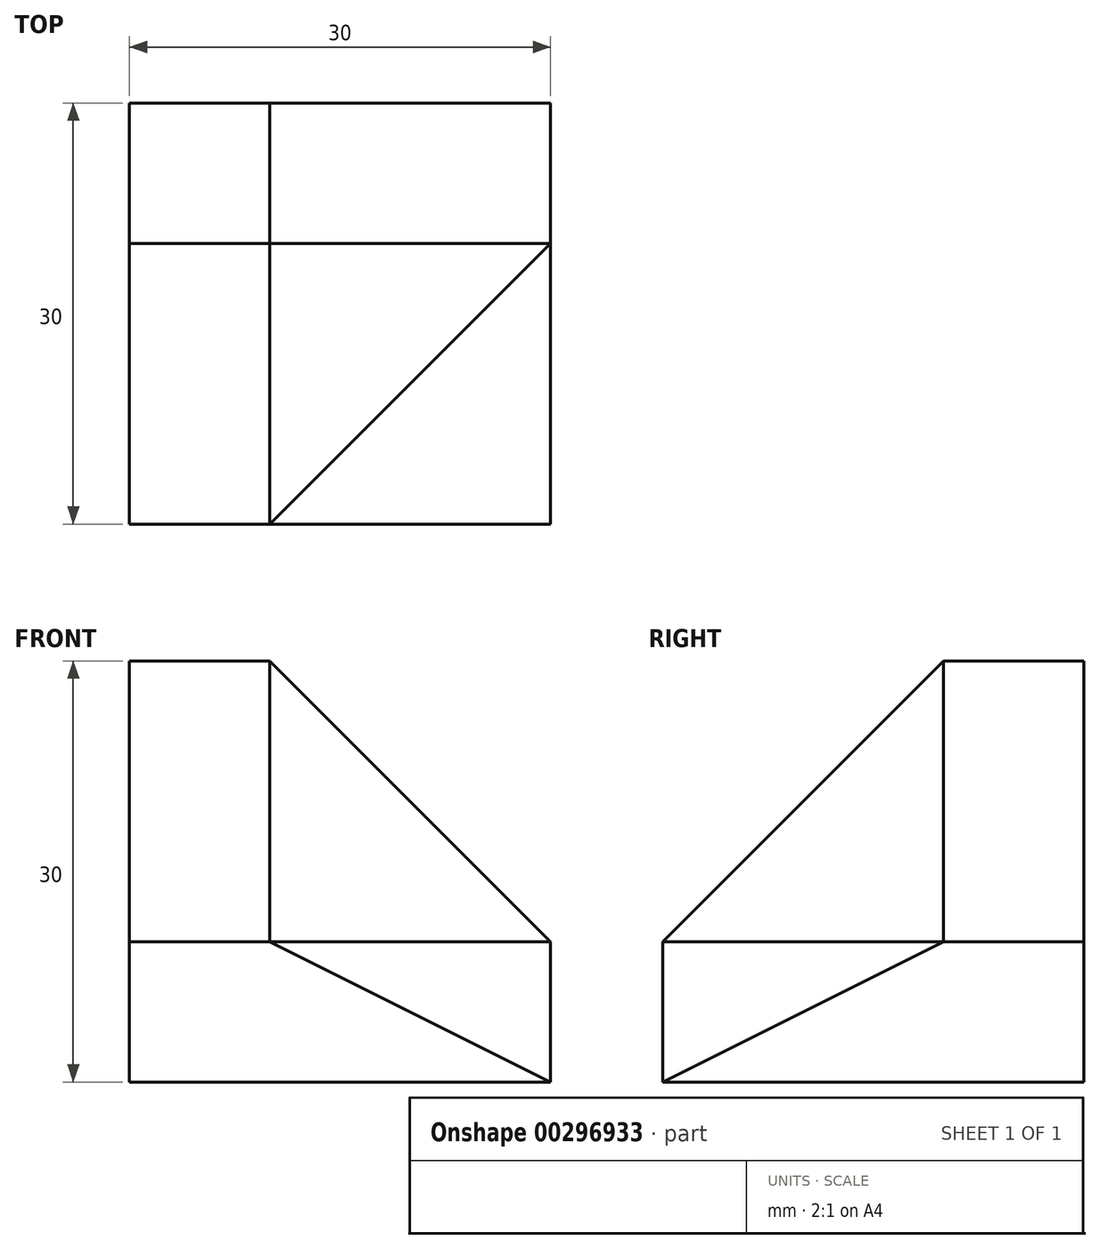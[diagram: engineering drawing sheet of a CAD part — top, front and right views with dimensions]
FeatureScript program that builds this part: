
annotation { "Feature Type Name" : "Feature", "Feature Type Description" : "" }
export const myFeature = defineFeature(function(context is Context, id is Id, definition is map)
    precondition{}
    {
        {
            var Q0;
            Q0=qCreatedBy(makeId("Front.planeOp"),FACE);
            var sketch = newSketch(context, id + "F0", { "sketchPlane" : qUnion([Q0])});
            skLineSegment(sketch, "E0.bottom", {"start": v(0, 0) * mm, "end": v(30, 0) * mm});
            skLineSegment(sketch, "E0.top", {"start": v(0, 30) * mm, "end": v(30, 30) * mm});
            skLineSegment(sketch, "E0.left", {"start": v(0, 0) * mm, "end": v(0, 30) * mm});
            skLineSegment(sketch, "E0.right", {"start": v(30, 0) * mm, "end": v(30, 30) * mm});
            skLineSegment(sketch, "E1", {"start": v(10, 30) * mm, "end": v(30, 10) * mm});
            skLineSegment(sketch, "E2.bottom", {"start": v(30, 30) * mm, "end": v(10, 30) * mm});
            skLineSegment(sketch, "E2.top", {"start": v(30, 10) * mm, "end": v(10, 10) * mm});
            skLineSegment(sketch, "E2.left", {"start": v(30, 30) * mm, "end": v(30, 10) * mm});
            skLineSegment(sketch, "E2.right", {"start": v(10, 30) * mm, "end": v(10, 10) * mm});
            skSolve(sketch);
        }
        {
            var Q0;
            {var subQ1=sQuery(id+"F0.wireOp",EDGE,"E0.bottom");Q0=makeQuery(id+"F0.imprint","IMPRINT",FACE,{"disambiguationData":[TD([[makeQuery(id+"F0.imprint","IMPRINT",EDGE,{"derivedFrom":subQ1}),1.0]])]});}
            var Q1;
            Q1=makeQuery(id+"F0.imprint","IMPRINT",FACE,{"disambiguationData":[TD([[makeQuery(id+"F0.imprint","IMPRINT",EDGE,{"derivedFrom":sQuery(id+"F0.wireOp",EDGE,"E1")}),-1.0]])]});
            extrude(context, id + "F1", {"entities" : qUnion([Q0, Q1]), "oppositeDirection" : true, "depth" : 30 * mm});
        }
        {
            var Q0;
            Q0=makeQuery(id+"F0.imprint","IMPRINT",FACE,{"disambiguationData":[TD([[makeQuery(id+"F0.imprint","IMPRINT",EDGE,{"derivedFrom":sQuery(id+"F0.wireOp",EDGE,"E1")}),-1.0]])]});
            extrude(context, id + "F2", {"entities" : qUnion([Q0]), "operationType" : NewBodyOperationType.REMOVE, "oppositeDirection" : true, "depth" : 20 * mm});
        }
        {
            var Q0;
            Q0=makeQuery(id+"F2.boolean.opBoolean","COPY",FACE,{"derivedFrom":makeQuery(id+"F2.opExtrude","SWEPT_FACE",FACE,{"disambiguationData":[OSD([sQuery(id+"F0.wireOp",EDGE,"E2.right")])]})});
            var sketch = newSketch(context, id + "F3", { "sketchPlane" : qUnion([Q0])});
            skLineSegment(sketch, "E3", {"start": v(20, 30) * mm, "end": v(0, 10) * mm});
            skSolve(sketch);
        }
        {
            var Q0;
            Q0 = qSketchRegion(id + "F3", true);
            var Q1;
            Q1=makeQuery(id+"F3.imprint","IMPRINT",FACE,{"disambiguationData":[TD([[makeQuery(id+"F3.imprint","IMPRINT",EDGE,{"derivedFrom":sQuery(id+"F3.wireOp",EDGE,"E3")}),-1.0]])]});
            extrude(context, id + "F4", {"entities" : qUnion([Q0, Q1]), "operationType" : NewBodyOperationType.REMOVE, "endBound" : BoundingType.THROUGH_ALL, "oppositeDirection" : true, "depth" : 25 * mm});
        }
        {
            var Q0;
            Q0=makeQuery(id+"F2.boolean.opBoolean","COPY",VERTEX,{"derivedFrom":makeQuery(id+"F2.opExtrude","CAP_VERTEX",VERTEX,{"disambiguationData":[OSD([sQuery(id+"F0.wireOp",EDGE,"E0.right"),sQuery(id+"F0.wireOp",EDGE,"E1"),sQuery(id+"F0.wireOp",EDGE,"E2.top"),sQuery(id+"F0.wireOp",EDGE,"E2.left")])],"isStart":false})});
            var Q1;
            {var subQ0=sQuery(id+"F0.wireOp",EDGE,"E2.right");var subQ1=sQuery(id+"F0.wireOp",EDGE,"E2.top");Q1=makeQuery(id+"F4.boolean.opBoolean","MERGE",VERTEX,{"derivedFrom":[makeQuery(id+"F2.boolean.opBoolean","COPY",VERTEX,{"derivedFrom":makeQuery(id+"F2.opExtrude","CAP_VERTEX",VERTEX,{"disambiguationData":[OSD([subQ1,subQ0])],"isStart":true})}),makeQuery(id+"F4.opExtrude","CAP_VERTEX",VERTEX,{"disambiguationData":[OSD([subQ1,subQ0,sQuery(id+"F3.wireOp",EDGE,"E3")])],"isStart":true})]});}
            var Q2;
            Q2=makeQuery(id+"F1.opExtrude","CAP_VERTEX",VERTEX,{"disambiguationData":[OSD([sQuery(id+"F0.wireOp",EDGE,"E0.bottom"),sQuery(id+"F0.wireOp",EDGE,"E0.right")])],"isStart":true});
            cPlane(context, id + "F5", {"entities" : qUnion([Q0, Q1, Q2]), "cplaneType" : CPlaneType.THREE_POINT, "offset" : 25 * mm, "width" : 150 * mm, "height" : 150 * mm});
        }
        {
            var Q0;
            Q0=qCreatedBy(id+"F5.planeOp",FACE);
            var sketch = newSketch(context, id + "F6", { "sketchPlane" : qUnion([Q0])});
            skPoint(sketch, "E4.0", {"position": v(27.39, -22.36) * mm});
            skPoint(sketch, "E5.0", {"position": v(5.48, -4.47) * mm});
            skPoint(sketch, "E6.0", {"position": v(27.39, 0) * mm});
            skLineSegment(sketch, "E7", {"start": v(27.39, -22.36) * mm, "end": v(5.48, -4.47) * mm});
            skLineSegment(sketch, "E8", {"start": v(27.39, 0) * mm, "end": v(5.48, -4.47) * mm});
            skLineSegment(sketch, "E9", {"start": v(27.39, -22.36) * mm, "end": v(27.39, 0) * mm});
            skSolve(sketch);
        }
        {
            var Q0;
            Q0 = qSketchRegion(id + "F6", true);
            extrude(context, id + "F7", {"entities" : qUnion([Q0]), "operationType" : NewBodyOperationType.REMOVE, "endBound" : BoundingType.THROUGH_ALL, "oppositeDirection" : true, "depth" : 25 * mm});
        }
    });
